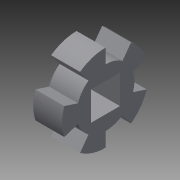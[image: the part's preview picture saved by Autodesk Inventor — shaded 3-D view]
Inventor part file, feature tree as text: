
AUTODESK INVENTOR PART (.ipt)
format: ipt  version: 2015 (Build 190159000, 159)  size: 103,936 bytes
history: native  units: in
note: dims shown in document units (in); Inventor stores cm internally (conversion verified against a paired STEP export)
features: extrude x1, sketch x1
ambient origin geometry x8: Origin, YZ Plane, XZ Plane, XY Plane, X Axis, Y Axis, Z Axis, Center Point
bodies: Solid1 (feature_tree)
feature tree (2):
  extrude  "Extrusion1"  Depth=0.05in
  sketch  "Sketch1"  dims[d0=0.05in d1=0.05in d3=0.15in d4=1.4842in d6=0.7421in d7=3.937in d9=360.0deg d11=0.05in d12=0.0in]
